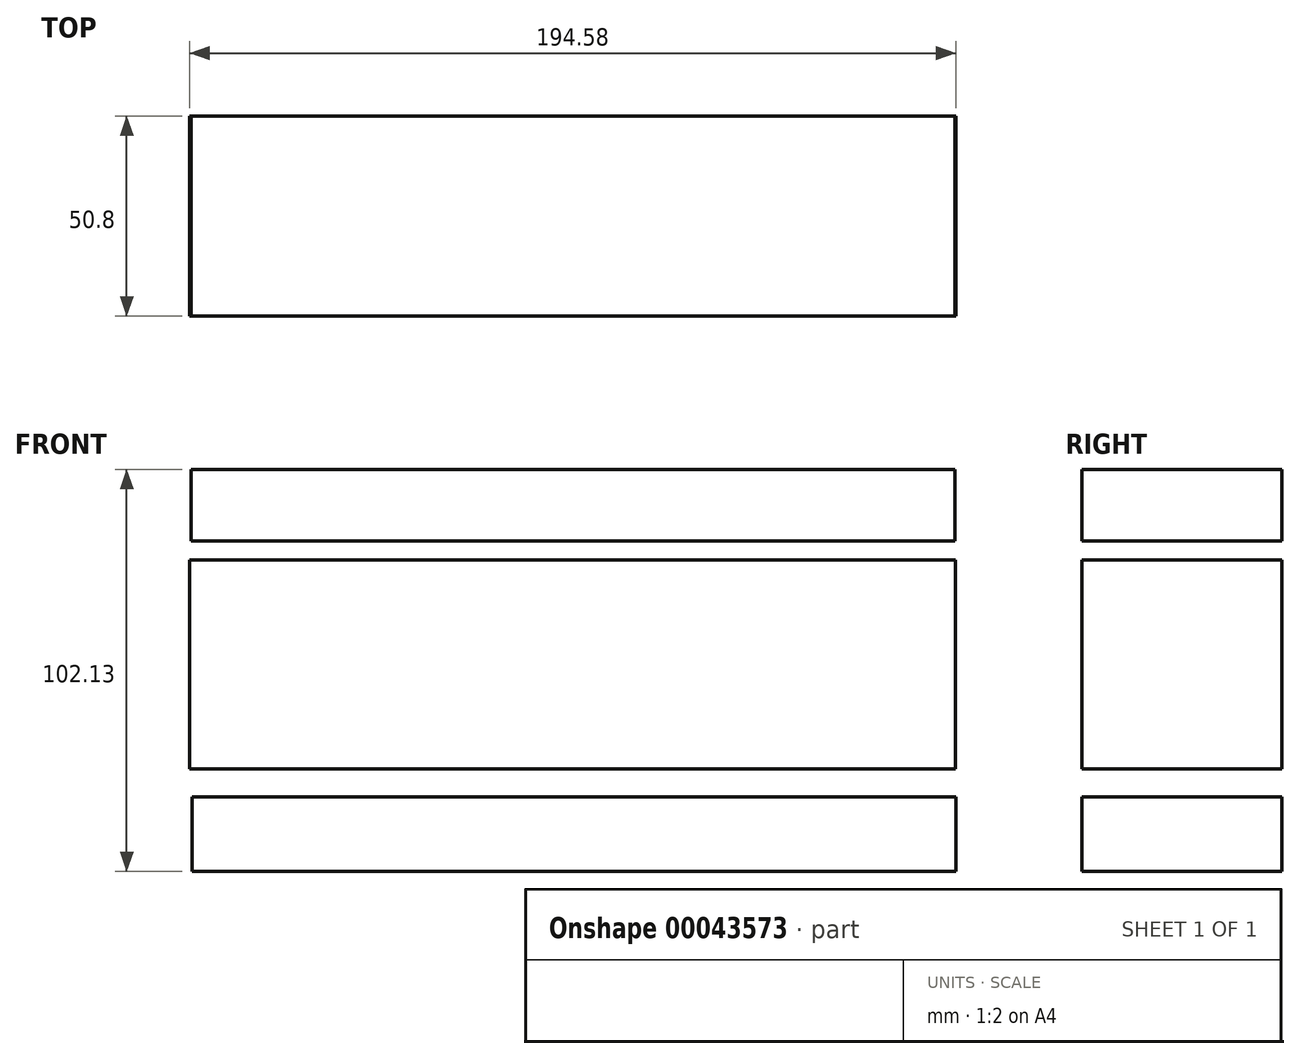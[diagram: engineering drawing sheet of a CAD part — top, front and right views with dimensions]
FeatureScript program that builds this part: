
annotation { "Feature Type Name" : "Feature", "Feature Type Description" : "" }
export const myFeature = defineFeature(function(context is Context, id is Id, definition is map)
    precondition{}
    {
        {
            var Q0;
            Q0=qCreatedBy(makeId("Front.planeOp"),FACE);
            var sketch = newSketch(context, id + "F0", { "sketchPlane" : qUnion([Q0])});
            skLineSegment(sketch, "E0.bottom", {"start": v(-94.72, 37.91) * mm, "end": v(99.74, 37.91) * mm});
            skLineSegment(sketch, "E0.top", {"start": v(-94.72, -15.19) * mm, "end": v(99.74, -15.19) * mm});
            skLineSegment(sketch, "E0.left", {"start": v(-94.72, 37.91) * mm, "end": v(-94.72, -15.19) * mm});
            skLineSegment(sketch, "E0.right", {"start": v(99.74, 37.91) * mm, "end": v(99.74, -15.19) * mm});
            skLineSegment(sketch, "E1", {"start": v(-94.72, 26.9) * mm, "end": v(99.74, 26.9) * mm});
            skLineSegment(sketch, "E2", {"start": v(-94.72, 0) * mm, "end": v(99.74, 0) * mm});
            skSolve(sketch);
        }
        {
            var Q0;
            {var subQ2=sQuery(id+"F0.wireOp",EDGE,"E0.top");Q0=makeQuery(id+"F0.imprint","IMPRINT",FACE,{"disambiguationData":[TD([[makeQuery(id+"F0.imprint","IMPRINT",EDGE,{"derivedFrom":subQ2}),1.0]])]});}
            var Q1;
            Q1 = qSketchRegion(id + "F0", true);
            extrude(context, id + "F1", {"entities" : qUnion([Q0, Q1]), "depth" : 50.8 * mm});
        }
        {
            var Q0;
            Q0=qCreatedBy(makeId("Front.planeOp"),FACE);
            var sketch = newSketch(context, id + "F2", { "sketchPlane" : qUnion([Q0])});
            skLineSegment(sketch, "E3.bottom", {"start": v(-94.36, 42.7) * mm, "end": v(99.62, 42.7) * mm});
            skLineSegment(sketch, "E3.top", {"start": v(-94.36, 60.87) * mm, "end": v(99.62, 60.87) * mm});
            skLineSegment(sketch, "E3.left", {"start": v(-94.36, 42.7) * mm, "end": v(-94.36, 60.87) * mm});
            skLineSegment(sketch, "E3.right", {"start": v(99.62, 42.7) * mm, "end": v(99.62, 60.87) * mm});
            skLineSegment(sketch, "E4.bottom", {"start": v(-94.12, -22.36) * mm, "end": v(99.86, -22.36) * mm});
            skLineSegment(sketch, "E4.top", {"start": v(-94.12, -41.26) * mm, "end": v(99.86, -41.26) * mm});
            skLineSegment(sketch, "E4.left", {"start": v(-94.12, -22.36) * mm, "end": v(-94.12, -41.26) * mm});
            skLineSegment(sketch, "E4.right", {"start": v(99.86, -22.36) * mm, "end": v(99.86, -41.26) * mm});
            skSolve(sketch);
        }
        {
            var Q0;
            Q0 = qSketchRegion(id + "F2", true);
            extrude(context, id + "F3", {"entities" : qUnion([Q0]), "depth" : 50.8 * mm});
        }
    });
